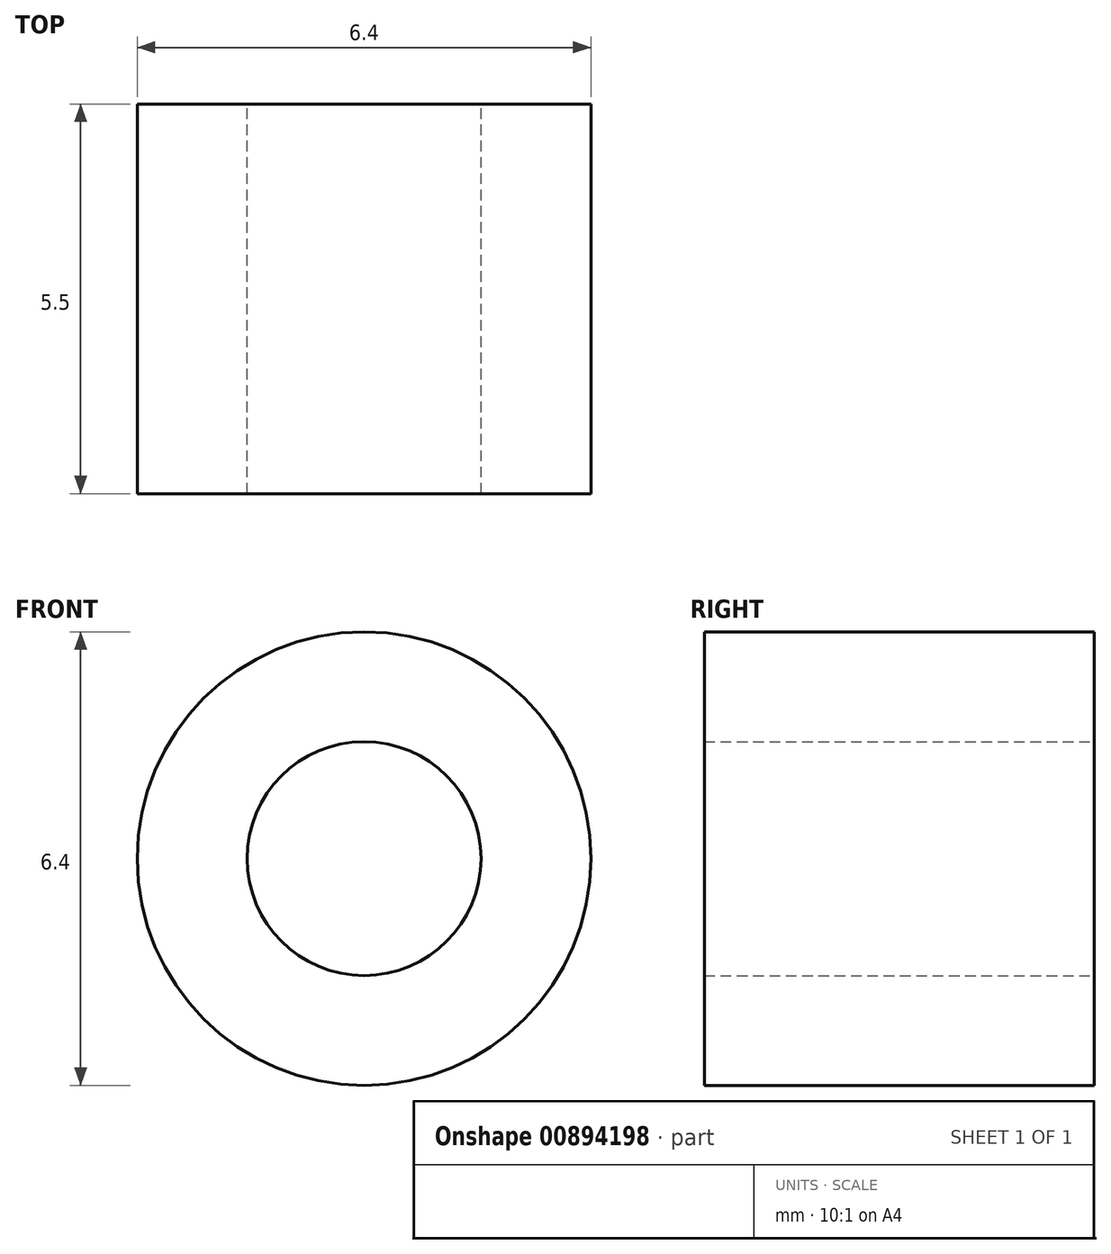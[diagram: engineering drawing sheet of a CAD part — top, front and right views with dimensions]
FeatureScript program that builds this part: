
annotation { "Feature Type Name" : "Feature", "Feature Type Description" : "" }
export const myFeature = defineFeature(function(context is Context, id is Id, definition is map)
    precondition{}
    {
        {
            var Q0;
            Q0=qCreatedBy(makeId("Front.planeOp"),FACE);
            var sketch = newSketch(context, id + "F0", { "sketchPlane" : qUnion([Q0])});
            skCircle(sketch, "E0", {"center": v(0, 0) * mm, "radius": 1.65 * mm});
            skCircle(sketch, "E1", {"center": v(0, 0) * mm, "radius": 3.2 * mm});
            skSolve(sketch);
        }
        {
            var Q0;
            Q0=makeQuery(id+"F0.imprint","IMPRINT",FACE,{"disambiguationData":[TD([[makeQuery(id+"F0.imprint","IMPRINT",EDGE,{"derivedFrom":sQuery(id+"F0.wireOp",EDGE,"E0")}),-1.0]])]});
            extrude(context, id + "F1", {"entities" : qUnion([Q0]), "depth" : 5.5 * mm, "offsetDistance" : 25 * mm});
        }
    });
